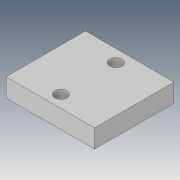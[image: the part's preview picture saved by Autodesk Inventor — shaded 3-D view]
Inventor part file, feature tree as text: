
AUTODESK INVENTOR PART (.ipt)
format: ipt  version: 2019 (Build 230136000, 136)  size: 91,136 bytes
history: native  units: mm
features: extrude x2, sketch x2
ambient origin geometry x8: Origin, YZ Plane, XZ Plane, XY Plane, X Axis, Y Axis, Z Axis, Center Point
bodies: Solid1 (feature_tree)
feature tree (4):
  extrude  "Extrusion1"  Depth=13.0mm
  extrude  "Extrusion2"  Depth=3.0mm
  sketch  "Sketch1"  dims[d0=14.5mm d1=13.0mm]
  sketch  "Sketch2"  dims[d2=3.0mm d3=0.0mm d4=2.0mm d5=2.0mm d6=2.0mm d7=7.0mm d8=7.0mm d9=2.0mm d10=3.0mm d11=0.0mm]
